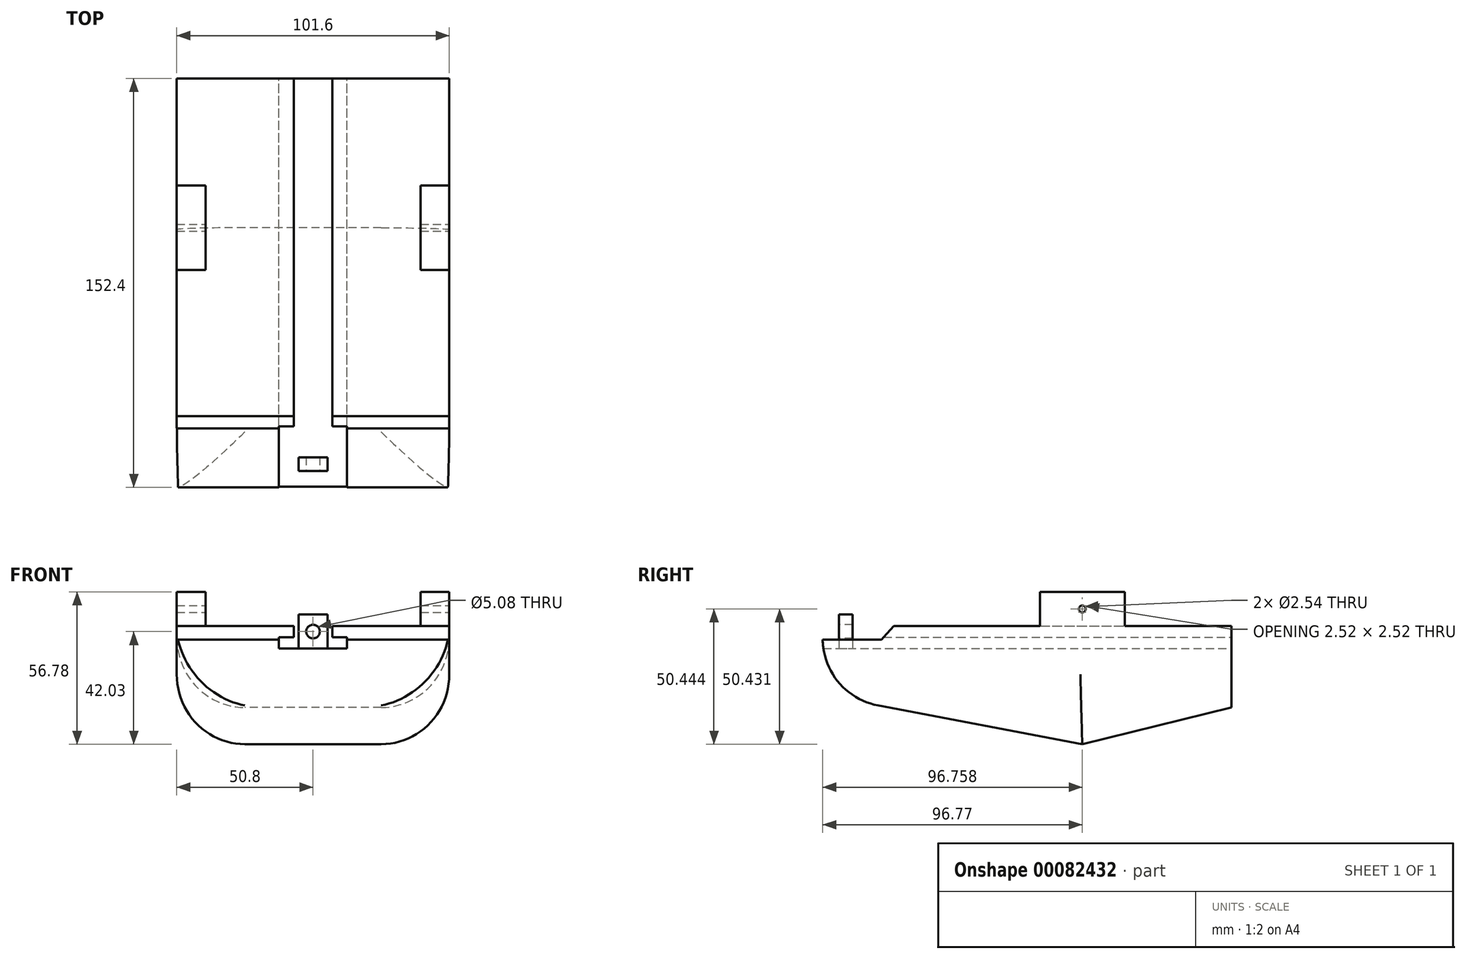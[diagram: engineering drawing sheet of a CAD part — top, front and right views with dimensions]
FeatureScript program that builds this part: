
annotation { "Feature Type Name" : "Feature", "Feature Type Description" : "" }
export const myFeature = defineFeature(function(context is Context, id is Id, definition is map)
    precondition{}
    {
        {
            var Q0;
            Q0=qCreatedBy(makeId("Right.planeOp"),FACE);
            var sketch = newSketch(context, id + "F0", { "sketchPlane" : qUnion([Q0])});
            skLineSegment(sketch, "E0", {"start": v(-96.77, 25.28) * mm, "end": v(-96.77, 4.64) * mm});
            skLineSegment(sketch, "E1", {"start": v(-96.77, 4.64) * mm, "end": v(0, -13.72) * mm});
            skLineSegment(sketch, "E2", {"start": v(0, -13.72) * mm, "end": v(55.63, 0) * mm});
            skLineSegment(sketch, "E3", {"start": v(55.63, 0) * mm, "end": v(55.63, 30.36) * mm});
            skLineSegment(sketch, "E4", {"start": v(55.63, 30.36) * mm, "end": v(-70.26, 30.36) * mm});
            skLineSegment(sketch, "E5", {"start": v(-70.26, 30.36) * mm, "end": v(-74.8, 25.28) * mm});
            skLineSegment(sketch, "E6", {"start": v(-74.8, 25.28) * mm, "end": v(-96.77, 25.28) * mm});
            skSolve(sketch);
        }
        {
            var Q0;
            Q0=makeQuery(id+"F0.imprint","IMPRINT",FACE,{"disambiguationData":[TD([[makeQuery(id+"F0.imprint","IMPRINT",EDGE,{"derivedFrom":sQuery(id+"F0.wireOp",EDGE,"E0")}),1.0]])]});
            extrude(context, id + "F1", {"entities" : qUnion([Q0]), "depth" : 101.6 * mm});
        }
        {
            var Q0;
            Q0=makeQuery(id+"F1.opExtrude","CAP_EDGE",EDGE,{"disambiguationData":[OSD([sQuery(id+"F0.wireOp",EDGE,"E1")])],"isStart":false});
            var Q1;
            Q1=makeQuery(id+"F1.opExtrude","CAP_EDGE",EDGE,{"disambiguationData":[OSD([sQuery(id+"F0.wireOp",EDGE,"E2")])],"isStart":false});
            var Q2;
            Q2=makeQuery(id+"F1.opExtrude","CAP_EDGE",EDGE,{"disambiguationData":[OSD([sQuery(id+"F0.wireOp",EDGE,"E2")])],"isStart":true});
            var Q3;
            Q3=makeQuery(id+"F1.opExtrude","CAP_EDGE",EDGE,{"disambiguationData":[OSD([sQuery(id+"F0.wireOp",EDGE,"E1")])],"isStart":true});
            var Q4;
            Q4=makeQuery(id+"F1.opExtrude","SWEPT_EDGE",EDGE,{"disambiguationData":[OSD([sQuery(id+"F0.wireOp",EDGE,"E0"),sQuery(id+"F0.wireOp",EDGE,"E1")])]});
            fillet(context, id + "F2", {"entities" : qUnion([Q0, Q1, Q2, Q3, Q4]), "radius" : 25.4 * mm, "tangentPropagation" : true, "allowEdgeOverflow" : false});
        }
        {
            var Q0;
            Q0=makeQuery(id+"F1.opExtrude","SWEPT_FACE",FACE,{"disambiguationData":[OSD([sQuery(id+"F0.wireOp",EDGE,"E4")])]});
            var sketch = newSketch(context, id + "F3", { "sketchPlane" : qUnion([Q0])});
            skLineSegment(sketch, "E7.bottom", {"start": v(10.73, -15.8) * mm, "end": v(0, -15.8) * mm});
            skLineSegment(sketch, "E7.top", {"start": v(10.73, 15.8) * mm, "end": v(0, 15.8) * mm});
            skLineSegment(sketch, "E7.left", {"start": v(10.73, -15.8) * mm, "end": v(10.73, 15.8) * mm});
            skLineSegment(sketch, "E7.right", {"start": v(0, -15.8) * mm, "end": v(0, 15.8) * mm});
            skPoint(sketch, "E7.middle", {"position": v(5.37, 0) * mm});
            skLineSegment(sketch, "E8", {"start": v(50.8, 55.63) * mm, "end": v(50.8, -105.48) * mm, "construction": true});
            skLineSegment(sketch, "E9.MirrorCS", {"start": v(90.87, 15.8) * mm, "end": v(101.6, 15.8) * mm});
            skLineSegment(sketch, "E10.MirrorCS", {"start": v(90.87, -15.8) * mm, "end": v(90.87, 15.8) * mm});
            skLineSegment(sketch, "E11.MirrorCS", {"start": v(90.87, -15.8) * mm, "end": v(101.6, -15.8) * mm});
            skLineSegment(sketch, "E12.MirrorCS", {"start": v(101.6, -15.8) * mm, "end": v(101.6, 15.8) * mm});
            skSolve(sketch);
        }
        {
            var Q0;
            Q0 = qSketchRegion(id + "F3", true);
            extrude(context, id + "F4", {"entities" : qUnion([Q0]), "operationType" : NewBodyOperationType.ADD, "depth" : 12.7 * mm});
        }
        {
            var Q0;
            Q0=makeQuery(id+"F1.opExtrude","SWEPT_FACE",FACE,{"disambiguationData":[OSD([sQuery(id+"F0.wireOp",EDGE,"E3")])]});
            var sketch = newSketch(context, id + "F5", { "sketchPlane" : qUnion([Q0])});
            skLineSegment(sketch, "E13.bottom", {"start": v(-38.1, 30.36) * mm, "end": v(-63.5, 30.36) * mm});
            skLineSegment(sketch, "E13.top", {"start": v(-38.1, 21.96) * mm, "end": v(-63.5, 21.96) * mm});
            skLineSegment(sketch, "E13.left", {"start": v(-38.1, 30.36) * mm, "end": v(-38.1, 21.96) * mm});
            skLineSegment(sketch, "E13.right", {"start": v(-63.5, 30.36) * mm, "end": v(-63.5, 21.96) * mm});
            skPoint(sketch, "E13.middle", {"position": v(-50.8, 26.16) * mm});
            skLineSegment(sketch, "E14", {"start": v(-63.5, 26.16) * mm, "end": v(-57.95, 26.16) * mm});
            skLineSegment(sketch, "E15", {"start": v(-57.95, 26.16) * mm, "end": v(-57.95, 30.36) * mm});
            skLineSegment(sketch, "E16", {"start": v(-57.95, 30.36) * mm, "end": v(-63.5, 30.36) * mm});
            skLineSegment(sketch, "E17", {"start": v(-63.5, 26.16) * mm, "end": v(-63.5, 30.36) * mm});
            skLineSegment(sketch, "E18", {"start": v(-50.8, 0) * mm, "end": v(-50.8, 43.17) * mm, "construction": true});
            skLineSegment(sketch, "E19.MirrorCS", {"start": v(-43.65, 26.16) * mm, "end": v(-43.65, 30.36) * mm});
            skLineSegment(sketch, "E20.MirrorCS", {"start": v(-38.1, 26.16) * mm, "end": v(-43.65, 26.16) * mm});
            skLineSegment(sketch, "E21.MirrorCS", {"start": v(-38.1, 26.16) * mm, "end": v(-38.1, 30.36) * mm});
            skLineSegment(sketch, "E22", {"start": v(-57.95, 30.36) * mm, "end": v(-43.65, 30.36) * mm});
            skSolve(sketch);
        }
        {
            var Q0;
            Q0=makeQuery(id+"F5.imprint","IMPRINT",FACE,{"disambiguationData":[TD([[makeQuery(id+"F5.imprint","IMPRINT",EDGE,{"derivedFrom":sQuery(id+"F5.wireOp",EDGE,"E13.top")}),-1.0]])]});
            extrude(context, id + "F6", {"entities" : qUnion([Q0]), "operationType" : NewBodyOperationType.REMOVE, "oppositeDirection" : true, "depth" : 203.2 * mm});
        }
        {
            var Q0;
            Q0=makeQuery(id+"F4.opExtrude","SWEPT_FACE",FACE,{"disambiguationData":[OSD([sQuery(id+"F3.wireOp",EDGE,"E12.MirrorCS")])]});
            var sketch = newSketch(context, id + "F7", { "sketchPlane" : qUnion([Q0])});
            skPoint(sketch, "E23", {"position": v(0, 36.71) * mm});
            skPoint(sketch, "E23.positionSnap0", {"position": v(15.8, 36.71) * mm});
            skPoint(sketch, "E23.positionSnap1", {"position": v(0, 43.06) * mm});
            skSolve(sketch);
        }
        {
            var Q0;
            Q0=sQuery(id+"F7.wireOp",VERTEX,"E23");
            var Q1;
            Q1=makeQuery(id+"F1.opExtrude","SWEPT_BODY",BODY,{"disambiguationData":[OSD([sQuery(id+"F0.wireOp",EDGE,"E0"),sQuery(id+"F0.wireOp",EDGE,"E1"),sQuery(id+"F0.wireOp",EDGE,"E2"),sQuery(id+"F0.wireOp",EDGE,"E3"),sQuery(id+"F0.wireOp",EDGE,"E4"),sQuery(id+"F0.wireOp",EDGE,"E5"),sQuery(id+"F0.wireOp",EDGE,"E6")])]});
            hole(context, id + "F8", {"style" : HoleStyle.C_BORE, "endStyle" : HoleEndStyle.THROUGH, "holeDiameter" : 2.54 * mm, "cBoreDiameter" : 2.54 * mm, "cBoreDepth" : 12.7 * mm, "locations" : qUnion([Q0]), "scope" : qUnion([Q1]), "isTappedThrough" : true});
        }
        {
            var Q0;
            Q0=makeQuery(id+"F6.boolean.opBoolean","COPY",FACE,{"derivedFrom":makeQuery(id+"F6.opExtrude","SWEPT_FACE",FACE,{"disambiguationData":[OSD([sQuery(id+"F5.wireOp",EDGE,"E13.top")])]})});
            var sketch = newSketch(context, id + "F9", { "sketchPlane" : qUnion([Q0])});
            skLineSegment(sketch, "E24.bottom", {"start": v(56.16, -90.65) * mm, "end": v(45.44, -90.65) * mm});
            skLineSegment(sketch, "E24.top", {"start": v(56.16, -85.57) * mm, "end": v(45.44, -85.57) * mm});
            skLineSegment(sketch, "E24.left", {"start": v(56.16, -90.65) * mm, "end": v(56.16, -85.57) * mm});
            skLineSegment(sketch, "E24.right", {"start": v(45.44, -90.65) * mm, "end": v(45.44, -85.57) * mm});
            skPoint(sketch, "E24.middle", {"position": v(50.8, -88.1) * mm});
            skPoint(sketch, "E24.middle.positionSnap0", {"position": v(50.8, -96.5) * mm});
            skPoint(sketch, "E24.centerSnap0", {"position": v(50.8, -96.5) * mm});
            skSolve(sketch);
        }
        {
            var Q0;
            Q0 = qSketchRegion(id + "F9", true);
            extrude(context, id + "F10", {"entities" : qUnion([Q0]), "operationType" : NewBodyOperationType.ADD, "depth" : 12.7 * mm});
        }
        {
            var Q0;
            Q0=makeQuery(id+"F10.opExtrude","SWEPT_FACE",FACE,{"disambiguationData":[OSD([sQuery(id+"F9.wireOp",EDGE,"E24.bottom")])]});
            var sketch = newSketch(context, id + "F11", { "sketchPlane" : qUnion([Q0])});
            skPoint(sketch, "E25", {"position": v(50.8, 28.31) * mm});
            skPoint(sketch, "E25.positionSnap0", {"position": v(56.16, 28.31) * mm});
            skPoint(sketch, "E25.positionSnap1", {"position": v(50.8, 34.66) * mm});
            skSolve(sketch);
        }
        {
            var Q0;
            Q0=sQuery(id+"F11.wireOp",VERTEX,"E25");
            var Q1;
            Q1=makeQuery(id+"F1.opExtrude","SWEPT_BODY",BODY,{"disambiguationData":[OSD([sQuery(id+"F0.wireOp",EDGE,"E0"),sQuery(id+"F0.wireOp",EDGE,"E1"),sQuery(id+"F0.wireOp",EDGE,"E2"),sQuery(id+"F0.wireOp",EDGE,"E3"),sQuery(id+"F0.wireOp",EDGE,"E4"),sQuery(id+"F0.wireOp",EDGE,"E5"),sQuery(id+"F0.wireOp",EDGE,"E6")])]});
            hole(context, id + "F12", {"style" : HoleStyle.C_BORE, "endStyle" : HoleEndStyle.THROUGH, "holeDiameter" : 5.08 * mm, "cBoreDiameter" : 5.08 * mm, "cBoreDepth" : 12.7 * mm, "locations" : qUnion([Q0]), "scope" : qUnion([Q1]), "isTappedThrough" : true});
        }
    });
